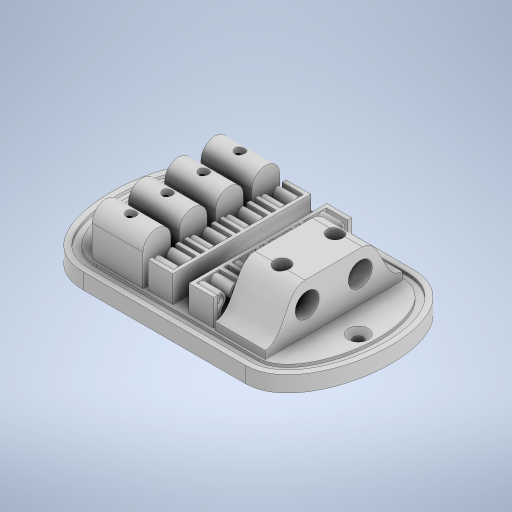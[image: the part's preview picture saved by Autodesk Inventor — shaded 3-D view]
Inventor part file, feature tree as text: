
AUTODESK INVENTOR PART (.ipt)
format: ipt  version: 2023 (Build 270158000, 158)  size: 819,200 bytes
history: native  units: in
note: dims shown in document units (in); Inventor stores cm internally (conversion verified against a paired STEP export)
features: extrude x10, sketch x9, plane x3, projected_geometry x3, mirror x1, pattern_linear x1, chamfer x1
ambient origin geometry x8: Origin, YZ Plane, XZ Plane, XY Plane, X Axis, Y Axis, Z Axis, Center Point
bodies: Body1 (feature_tree)
feature tree (28):
  extrude  "Extrusion2"  Depth=7.874in
  sketch  "Sketch4"  dims[d33=5.9055in d34=2.9528in]
  plane  "Work Plane1"
  sketch  "Sketch5"  dims[d35=3.937in d36=1.4862in]
  extrude  "Extrusion3"  Depth=2.9528in
  extrude  "Extrusion4"  Depth=1.4862in
  extrude  "Extrusion5"  Depth=0.9843in
  plane  "Work Plane2"
  extrude  "Extrusion6"  Depth=0.9843in
  plane  "Work Plane3"
  extrude  "Extrusion7"  Depth=0.1024in
  extrude  "Extrusion8"  Depth=1.5256in
  mirror  "Mirror1"
  sketch  "Sketch10"  dims[d41=0.2835in d42=0.0in d43=0.1024in]
  extrude  "Extrusion9"  Depth=2.4409in
  pattern_linear  "Rectangular Pattern1"  Spacing1=0.1378in  [1 undecoded]
  extrude  "Extrusion10"  Depth=1.0236in
  extrude  "Extrusion11"  Depth=0.5118in
  chamfer  "Chamfer1"  Distance=0.4272in
  sketch  "Sketch3"  dims[d31=2.9724in d32=7.874in]
  projected_geometry  "Projected Loop5"
  sketch  "Sketch6"  dims[d37=2.4272in d38=0.9843in]
  projected_geometry  "Projected Loop6"
  projected_geometry  "Projected Loop7"
  sketch  "Sketch9"  dims[d39=2.9724in d40=0.9843in]
  sketch  "Sketch11"  dims[d44=0.2264in d45=1.5256in]
  sketch  "Sketch12"  dims[d46=0.8701in d47=2.4409in]
  sketch  "Sketch13"  dims[d48=1.2205in d49=0.1378in d51=1.0236in d52=0.5118in d53=0.4272in d54=0.4724in d55=0.4724in d56=0.4006in d57=0.4006in d58=0.0492in d59=0.0in d60=0.8929in d61=0.0in d62=0.2756in d63=0.2756in d64=0.2756in d65=0.0in d66=1.2894in d67=0.498in d71=1.5748in d73=0.6457in d74=0.3937in d76=0.3937in d78=0.9055in d79=0.0in d80=0.7992in d81=0.1732in d86=1.5748in d88=0.6457in d89=0.3937in d91=0.3937in d93=0.2362in d94=0.0in d96=0.0709in d97=0.4134in d99=0.0787in d100=0.2913in d101=0.0472in d102=0.4429in d103=0.063in d104=0.3799in d105=0.4724in d106=0.0in d107=0.3543in d108=0.1181in d109=0.2362in d110=0.1181in d111=0.0591in d112=0.3543in d113=0.1772in d114=0.2362in d115=0.1181in d116=0.1772in d117=0.0886in d128=0.3543in d131=0.1181in d132=0.0787in d134=0.3543in d137=0.0197in d139=0.0197in d145=0.0197in d146=0.0197in d147=0.3543in d148=0.0in d149=1.5748in d151=0.6299in d152=0.7874in d154=0.7776in d155=0.5581in d156=0.315in d157=0.315in d158=0.315in d159=0.315in d160=0.3937in d161=0.0in d162=0.1772in d163=0.1772in d164=3.9291in d165=1.9646in d166=0.3937in d167=0.0in d168=0.0886in d169=0.0787in d170=45.0deg]
note: 1 required parameter value undecoded (feature->parameter linkage not recoverable at this tier; creation-order binding heuristic only, values carry confidence <= 0.55)
